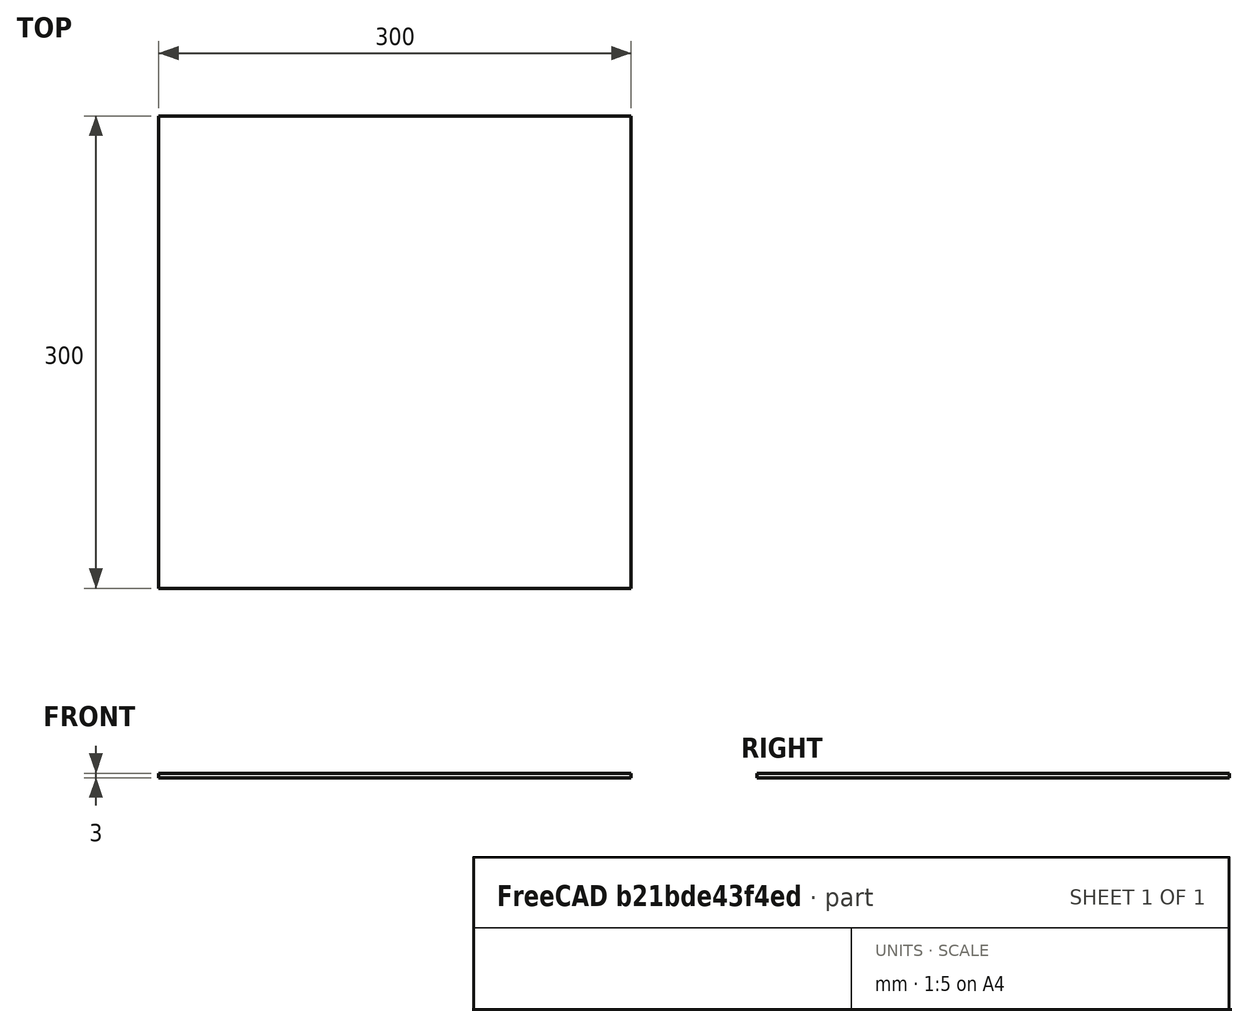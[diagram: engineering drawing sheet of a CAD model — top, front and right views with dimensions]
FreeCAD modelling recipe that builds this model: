
FCSTD DOCUMENT  (FreeCAD 0.19R23578 (Git))
Label: mirror_tile
License: All rights reserved
LicenseURL: http://en.wikipedia.org/wiki/All_rights_reserved
objects: Sketcher::SketchObject×1, PartDesign::Pad×1, PartDesign::Body×1, App::Part×1
note: 4 computed .brp shape members not serialized (recipe doc carries the construction recipe); baked Part::Feature solids carry a one-line shape summary decoded from their .brp

FEATURE [Sketcher::SketchObject] Sketch002
  MapMode = 5
  Support = -> [XY_Plane005]
  sketch-geometry (4):
    g0: LineSegment StartX=-150 StartY=150 StartZ=0 EndX=150 EndY=150 EndZ=0
    g1: LineSegment StartX=150 StartY=150 StartZ=0 EndX=150 EndY=-150 EndZ=0
    g2: LineSegment StartX=150 StartY=-150 StartZ=0 EndX=-150 EndY=-150 EndZ=0
    g3: LineSegment StartX=-150 StartY=-150 StartZ=0 EndX=-150 EndY=150 EndZ=0
  constraints (12):
    c: Coincident(g0,g1)
    c: Coincident(g1,g2)
    c: Coincident(g2,g3)
    c: Coincident(g3,g0)
    c: Horizontal(g0)
    c: Horizontal(g2)
    c: Vertical(g1)
    c: Vertical(g3)
    c: DistanceX(g0,g0) = 300
    c: DistanceY(g3,g3) = 300
    c: DistanceY(g-1,g0) = 150
    c: DistanceX(g-1,g0) = 150
FEATURE [PartDesign::Pad] Pad007
  AllowMultiFace = false
  Direction = (1,1,1)
  Length = 3
  Length2 = 100
  Profile = -> Sketch002
  Type = 0
  expr: Length = 3mm
FEATURE [PartDesign::Body] Body002
  Group = -> [Sketch002,Pad007]
  Origin = -> Origin005
  Tip = -> Pad007
FEATURE [App::Part] Part010  label="mirror_plate"
  Group = -> [Body002]
  Origin = -> Origin014
